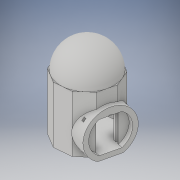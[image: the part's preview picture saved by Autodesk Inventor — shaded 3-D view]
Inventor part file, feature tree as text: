
AUTODESK INVENTOR PART (.ipt)
format: ipt  version: 2017 (Build 210142000, 142)  size: 381,440 bytes
history: native  units: in
note: dims shown in document units (in); Inventor stores cm internally (conversion verified against a paired STEP export)
features: extrude x10, sketch x8, other x4, mirror x1
ambient origin geometry x8: Origin, YZ Plane, XZ Plane, XY Plane, X Axis, Y Axis, Z Axis, Center Point
bodies: Solid1 (feature_tree), Solid2 (feature_tree)
feature tree (23):
  extrude  "bace"  Depth=1.0in TaperAngle=0.0deg
  extrude  "bace wall"  Depth=10.0in TaperAngle=0.0deg
  extrude  "bace cieiling"  Depth=2.0in
  other  "dome work plane"
  other  "dome"
  extrude  "door frame"  Depth=1.0in TaperAngle=0.0deg
  extrude  "corridor connection"  Depth=2.0in TaperAngle=0.0deg
  extrude  "hide sliding doors"  Depth=5.6918in
  extrude  "left door slot"  Depth=1.0in
  other  "door slot mirror"
  sketch  "Sketch12"  dims[d42=1.2585in d43=0.0in d44=4.0in d45=0.5833in d46=0.0625in d47=0.0625in d48=0.125in d52=0.25in d53=0.125in d54=45.0deg d55=0.0892in d56=0.0884in d57=1.0in d58=0.0in d59=1.0in d60=0.0in d61=1.0in d62=0.0in]
  extrude  "light"  Depth=1.0in TaperAngle=0.0deg
  extrude  "into wall light cut"  Depth=1.0in TaperAngle=0.0deg
  extrude  "into wall light join"  Depth=1.0in TaperAngle=0.0deg
  mirror  "Mirror1"
  other  "terminal connection parrale to door workplane"
  sketch  "Sketch1"  dims[d0=11.3835in d1=1.0in d2=0.0in]
  sketch  "Sketch2"  dims[d4=1.0in d5=10.0in d6=0.0in]
  sketch  "Sketch3"  dims[d8=1.0in d9=0.0in d16=2.0in d17=6.6667in]
  sketch  "Sketch8"  dims[d18=1.6875in d19=0.0in d20=1.0in d21=0.0in]
  sketch  "Sketch9"  dims[d22=0.25in d23=0.5in d24=6.6667in d25=2.0in d26=0.0in]
  sketch  "Sketch10"  dims[d32=4.6918in d33=5.6918in]
  sketch  "Sketch11"  dims[d34=90.0deg d38=1.0in]
